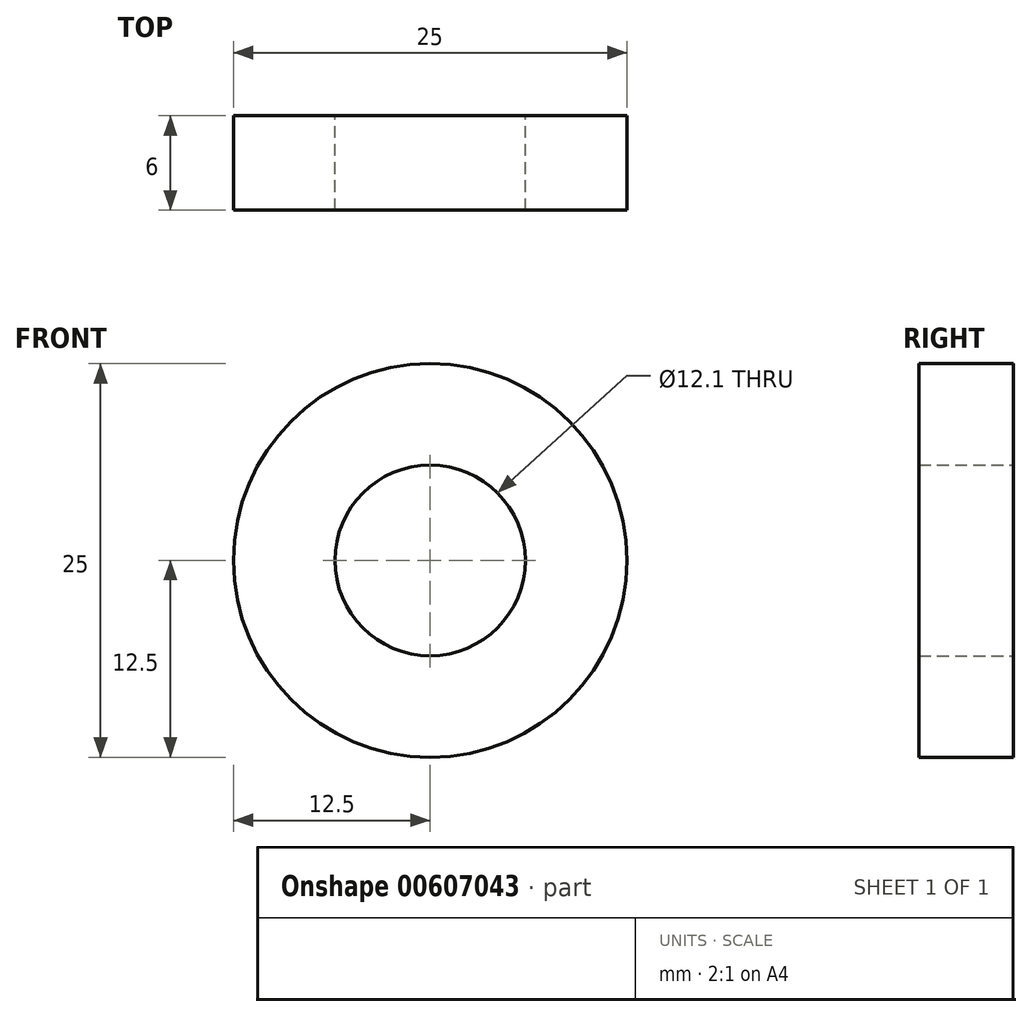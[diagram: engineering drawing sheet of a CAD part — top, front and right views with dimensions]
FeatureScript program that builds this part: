
annotation { "Feature Type Name" : "Feature", "Feature Type Description" : "" }
export const myFeature = defineFeature(function(context is Context, id is Id, definition is map)
    precondition{}
    {
        {
            var Q0;
            Q0=qCreatedBy(makeId("Front.planeOp"),FACE);
            var sketch = newSketch(context, id + "F0", { "sketchPlane" : qUnion([Q0]) });
            skCircle(sketch, "E0", {"center": v(0, 0) * mm, "radius": 12.5 * mm});
            skCircle(sketch, "E1", {"center": v(0, 0) * mm, "radius": 6.05 * mm});
            skSolve(sketch);
        }
        {
            var Q0;
            Q0=makeQuery(id+"F0.imprint","IMPRINT",FACE,{"disambiguationData":[TD([[makeQuery(id+"F0.imprint","IMPRINT",EDGE,{"derivedFrom":sQuery(id+"F0.wireOp",EDGE,"E0")}),1.0]])]});
            extrude(context, id + "F1", {"entities" : qUnion([Q0]), "depth" : 6 * mm, "offsetDistance" : 25 * mm});
        }
    });
